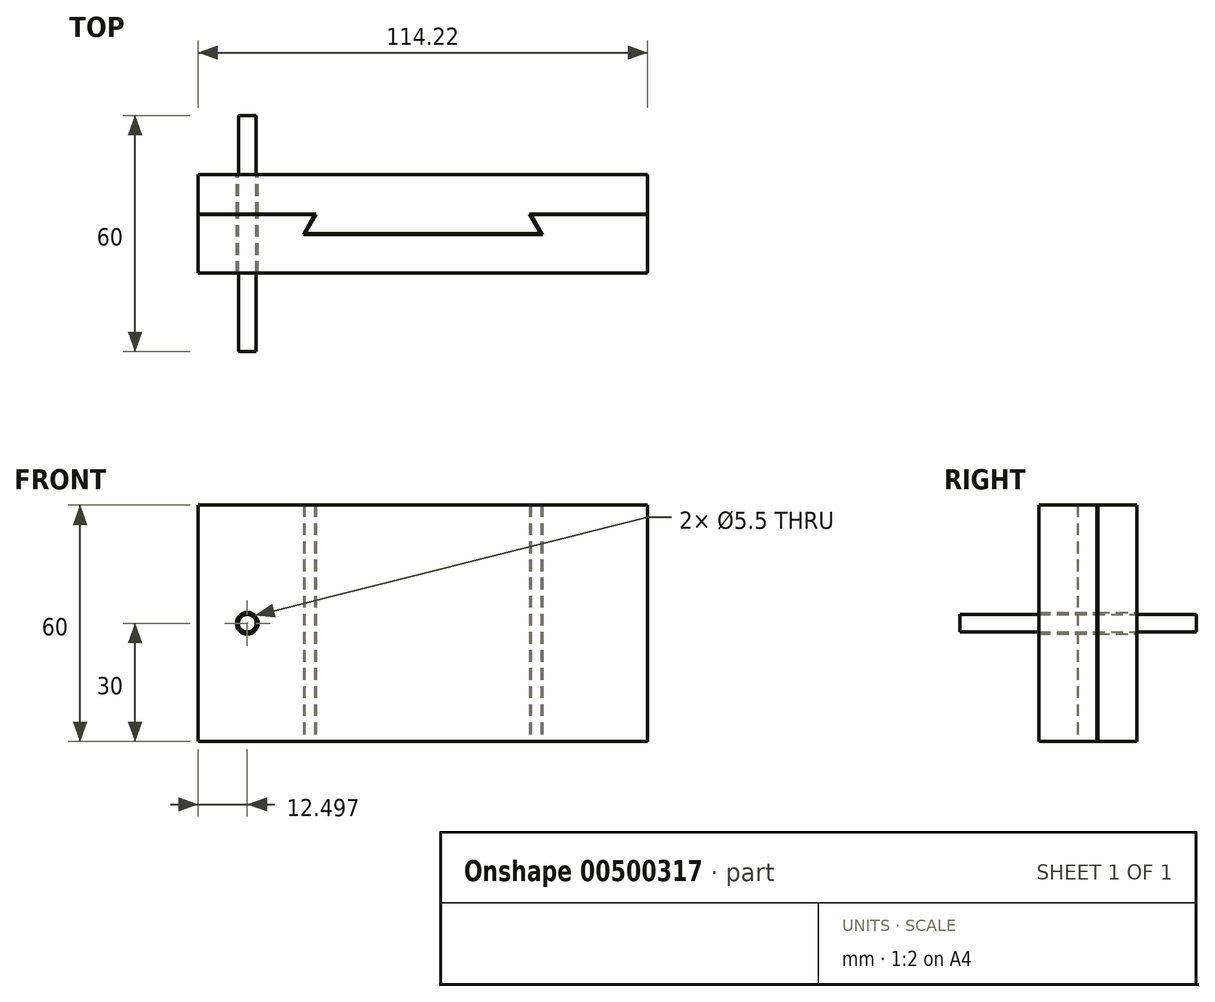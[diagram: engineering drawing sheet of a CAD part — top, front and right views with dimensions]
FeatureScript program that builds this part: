
annotation { "Feature Type Name" : "Feature", "Feature Type Description" : "" }
export const myFeature = defineFeature(function(context is Context, id is Id, definition is map)
    precondition{}
    {
        {
            var Q0;
            Q0=qCreatedBy(makeId("Top.planeOp"),FACE);
            var sketch = newSketch(context, id + "F0", { "sketchPlane" : qUnion([Q0])});
            skLineSegment(sketch, "E0", {"start": v(-57.11, 15) * mm, "end": v(-57.11, 5) * mm});
            skLineSegment(sketch, "E1", {"start": v(-57.11, 5) * mm, "end": v(-27.11, 5) * mm});
            skLineSegment(sketch, "E2", {"start": v(-27.11, 5) * mm, "end": v(-30, 0) * mm});
            skLineSegment(sketch, "E3", {"start": v(-30, 0) * mm, "end": v(0, 0) * mm});
            skLineSegment(sketch, "E4", {"start": v(0, 15) * mm, "end": v(0, 0) * mm, "construction": true});
            skLineSegment(sketch, "E5.MirrorCS", {"start": v(30, 0) * mm, "end": v(0, 0) * mm});
            skLineSegment(sketch, "E6.MirrorCS", {"start": v(57.11, 5) * mm, "end": v(27.11, 5) * mm});
            skLineSegment(sketch, "E7.MirrorCS", {"start": v(27.11, 5) * mm, "end": v(30, 0) * mm});
            skLineSegment(sketch, "E8.MirrorCS", {"start": v(57.11, 15) * mm, "end": v(57.11, 5) * mm});
            skLineSegment(sketch, "E9", {"start": v(-57.11, 15) * mm, "end": v(57.11, 15) * mm});
            skLineSegment(sketch, "E10.0", {"start": v(57.11, 4.8) * mm, "end": v(27.46, 4.8) * mm});
            skLineSegment(sketch, "E10.1", {"start": v(27.46, 4.8) * mm, "end": v(30.35, -0.2) * mm});
            skLineSegment(sketch, "E10.2", {"start": v(-57.11, 4.8) * mm, "end": v(-27.46, 4.8) * mm});
            skLineSegment(sketch, "E10.3", {"start": v(-27.46, 4.8) * mm, "end": v(-30.35, -0.2) * mm});
            skLineSegment(sketch, "E10.4", {"start": v(-30.35, -0.2) * mm, "end": v(0, -0.2) * mm});
            skLineSegment(sketch, "E10.5", {"start": v(30.35, -0.2) * mm, "end": v(0, -0.2) * mm});
            skLineSegment(sketch, "E11", {"start": v(-57.11, 5) * mm, "end": v(-57.11, -10) * mm});
            skLineSegment(sketch, "E12", {"start": v(-57.11, -10) * mm, "end": v(57.11, -10) * mm});
            skLineSegment(sketch, "E13", {"start": v(57.11, -10) * mm, "end": v(57.11, 4.8) * mm});
            skSolve(sketch);
        }
        {
            var Q0;
            Q0 = qSketchRegion(id + "F0", true);
            extrude(context, id + "F1", {"entities" : qUnion([Q0]), "depth" : 60 * mm});
        }
        {
            var Q0;
            Q0=makeQuery(id+"F1.opExtrude","SWEPT_FACE",FACE,{"disambiguationData":[OSD([sQuery(id+"F0.wireOp",EDGE,"E9")])]});
            var sketch = newSketch(context, id + "F2", { "sketchPlane" : qUnion([Q0])});
            skPoint(sketch, "E14", {"position": v(44.61, 30) * mm});
            skPoint(sketch, "E14.positionSnap0", {"position": v(57.11, 30) * mm});
            skSolve(sketch);
        }
        {
            var Q0;
            Q0=sQuery(id+"F2.wireOp",VERTEX,"E14");
            var Q1;
            Q1=makeQuery(id+"F1.opExtrude","SWEPT_BODY",BODY,{"disambiguationData":[OSD([sQuery(id+"F0.wireOp",EDGE,"E0"),sQuery(id+"F0.wireOp",EDGE,"E1"),sQuery(id+"F0.wireOp",EDGE,"E2"),sQuery(id+"F0.wireOp",EDGE,"E3"),sQuery(id+"F0.wireOp",EDGE,"E5.MirrorCS"),sQuery(id+"F0.wireOp",EDGE,"E6.MirrorCS"),sQuery(id+"F0.wireOp",EDGE,"E7.MirrorCS"),sQuery(id+"F0.wireOp",EDGE,"E8.MirrorCS"),sQuery(id+"F0.wireOp",EDGE,"E9")])]});
            var Q2;
            Q2=makeQuery(id+"F1.opExtrude","SWEPT_BODY",BODY,{"disambiguationData":[OSD([sQuery(id+"F0.wireOp",EDGE,"E10.0"),sQuery(id+"F0.wireOp",EDGE,"E10.1"),sQuery(id+"F0.wireOp",EDGE,"E10.2"),sQuery(id+"F0.wireOp",EDGE,"E10.3"),sQuery(id+"F0.wireOp",EDGE,"E10.4"),sQuery(id+"F0.wireOp",EDGE,"E10.5"),sQuery(id+"F0.wireOp",EDGE,"E11"),sQuery(id+"F0.wireOp",EDGE,"E12"),sQuery(id+"F0.wireOp",EDGE,"E13")])]});
            hole(context, id + "F3", {"style" : HoleStyle.SIMPLE, "endStyle" : HoleEndStyle.THROUGH, "standardTappedOrClearance" : lookupTablePath({ "standard" : "ISO", "fit" : "Normal", "size" : "M5", "type" : "Clearance" }), "standardBlindInLast" : lookupTablePath({ "fit" : "Standard", "standard" : "ISO", "size" : "M5", "type" : "Clearance" }), "holeDiameter" : 5.5 * mm, "isTappedThrough" : true, "tappedDepth" : 7 * mm, "tapClearance" : 6, "startFromSketch" : true, "locations" : qUnion([Q0]), "scope" : qUnion([Q1, Q2])});
        }
        {
            var Q0;
            Q0=qCreatedBy(makeId("Front.planeOp"),FACE);
            var sketch = newSketch(context, id + "F4", { "sketchPlane" : qUnion([Q0])});
            skCircle(sketch, "E15", {"center": v(-44.61, 30) * mm, "radius": 2.25 * mm});
            skSolve(sketch);
        }
        {
            var Q0;
            Q0 = qSketchRegion(id + "F4", true);
            extrude(context, id + "F5", {"entities" : qUnion([Q0]), "depth" : 60 * mm, "symmetric" : true});
        }
    });
